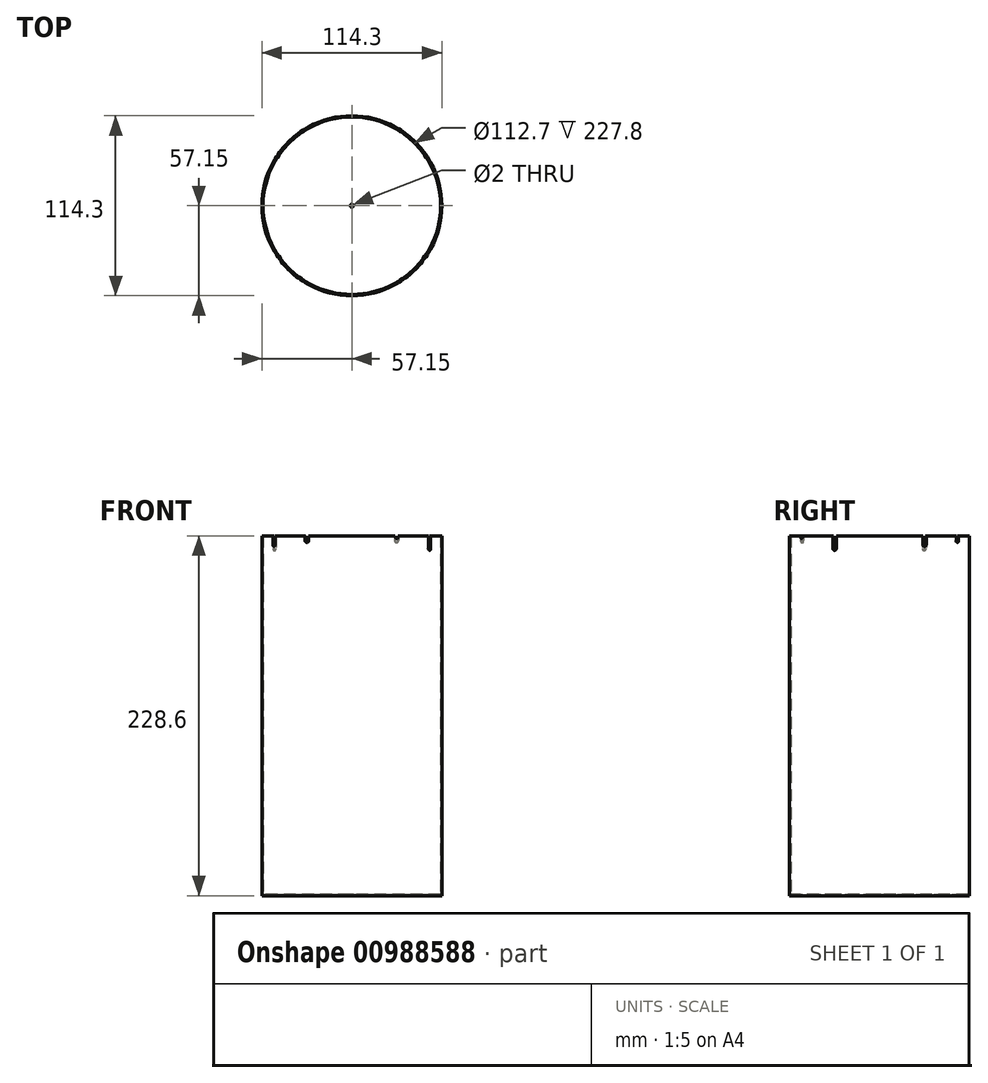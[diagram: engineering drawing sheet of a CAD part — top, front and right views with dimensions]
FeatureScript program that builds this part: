
annotation { "Feature Type Name" : "Feature", "Feature Type Description" : "" }
export const myFeature = defineFeature(function(context is Context, id is Id, definition is map)
    precondition{}
    {
        {
            var Q0;
            Q0=qCreatedBy(makeId("Top.planeOp"),FACE);
            var sketch = newSketch(context, id + "F0", { "sketchPlane" : qUnion([Q0])});
            skCircle(sketch, "E0", {"center": v(0, 0) * mm, "radius": 57.15 * mm});
            skSolve(sketch);
        }
        {
            var Q0;
            Q0=makeQuery(id+"F0.imprint","IMPRINT",FACE,{"disambiguationData":[TD([[makeQuery(id+"F0.imprint","IMPRINT",EDGE,{"derivedFrom":sQuery(id+"F0.wireOp",EDGE,"E0")}),1.0]])]});
            extrude(context, id + "F1", {"entities" : qUnion([Q0]), "depth" : 228.6 * mm, "offsetDistance" : 25.4 * mm});
        }
        {
            var Q0;
            Q0=makeQuery(id+"F1.opExtrude","CAP_FACE",FACE,{"disambiguationData":[OSD([sQuery(id+"F0.wireOp",EDGE,"E0")])],"isStart":false});
            shell(context, id + "F2", {"entities" : qUnion([Q0]), "thickness" : 0.8 * mm});
        }
        {
            var Q0;
            Q0=makeQuery(id+"F1.opExtrude","CAP_FACE",FACE,{"disambiguationData":[OSD([sQuery(id+"F0.wireOp",EDGE,"E0")])],"isStart":false});
            var sketch = newSketch(context, id + "F3", { "sketchPlane" : qUnion([Q0])});
            skLineSegment(sketch, "E1", {"start": v(-49.5, 28.57) * mm, "end": v(49.5, -28.57) * mm});
            skLineSegment(sketch, "E2", {"start": v(-49.5, -28.58) * mm, "end": v(49.5, 28.58) * mm});
            skLineSegment(sketch, "E3", {"start": v(-28.58, 49.5) * mm, "end": v(28.58, -49.5) * mm});
            skLineSegment(sketch, "E4", {"start": v(28.58, 49.5) * mm, "end": v(-28.58, -49.5) * mm});
            skSolve(sketch);
        }
        {
            var Q0;
            Q0=sQuery(id+"F3.wireOp",EDGE,"E3");
            var Q1;
            Q1=sQuery(id+"F3.wireOp",VERTEX,"E3.end");
            cPlane(context, id + "F4", {"entities" : qUnion([Q0, Q1]), "cplaneType" : CPlaneType.LINE_POINT, "offset" : 25.4 * mm, "width" : 152.4 * mm, "height" : 152.4 * mm});
        }
        {
            var Q0;
            Q0=sQuery(id+"F3.wireOp",EDGE,"E2");
            var Q1;
            Q1=sQuery(id+"F3.wireOp",VERTEX,"E2.start");
            cPlane(context, id + "F5", {"entities" : qUnion([Q0, Q1]), "cplaneType" : CPlaneType.LINE_POINT, "offset" : 25.4 * mm, "width" : 152.4 * mm, "height" : 152.4 * mm});
        }
        {
            var Q0;
            Q0=sQuery(id+"F3.wireOp",EDGE,"E1");
            var Q1;
            Q1=sQuery(id+"F3.wireOp",VERTEX,"E1.start");
            cPlane(context, id + "F6", {"entities" : qUnion([Q0, Q1]), "cplaneType" : CPlaneType.LINE_POINT, "offset" : 25.4 * mm, "width" : 152.4 * mm, "height" : 152.4 * mm});
        }
        {
            var Q0;
            Q0=sQuery(id+"F3.wireOp",EDGE,"E4");
            var Q1;
            Q1=sQuery(id+"F3.wireOp",VERTEX,"E4.end");
            cPlane(context, id + "F7", {"entities" : qUnion([Q0, Q1]), "cplaneType" : CPlaneType.LINE_POINT, "offset" : 25.4 * mm, "width" : 152.4 * mm, "height" : 152.4 * mm});
        }
        {
            var Q0;
            Q0=qCreatedBy(id+"F4.planeOp",FACE);
            var sketch = newSketch(context, id + "F8", { "sketchPlane" : qUnion([Q0])});
            skLineSegment(sketch, "E5", {"start": v(-1.25, 228.6) * mm, "end": v(-1.25, 228.1) * mm});
            skLineSegment(sketch, "E6", {"start": v(1.25, 228.6) * mm, "end": v(1.25, 228.1) * mm});
            skLineSegment(sketch, "E7", {"start": v(-1.25, 228.6) * mm, "end": v(1.25, 228.6) * mm});
            skArc(sketch, "E8", {"start": v(-1.25, 228.1) * mm, "mid": v(0, 226.85) * mm, "end": v(1.25, 228.1) * mm});
            skSolve(sketch);
        }
        {
            var Q0;
            Q0=makeQuery(id+"F8.imprint","IMPRINT",FACE,{"disambiguationData":[TD([[makeQuery(id+"F8.imprint","IMPRINT",EDGE,{"derivedFrom":sQuery(id+"F8.wireOp",EDGE,"E5")}),1.0]])]});
            var Q1;
            Q1=sQuery(id+"F3.wireOp",EDGE,"E3");
            sweep(context, id + "F9", {"operationType" : NewBodyOperationType.REMOVE, "profiles" : qUnion([Q0]), "path" : qUnion([Q1])});
        }
        {
            var Q0;
            Q0=qCreatedBy(id+"F7.planeOp",FACE);
            var sketch = newSketch(context, id + "F10", { "sketchPlane" : qUnion([Q0])});
            skLineSegment(sketch, "E9", {"start": v(-1.25, 228.6) * mm, "end": v(-1.25, 225.6) * mm});
            skLineSegment(sketch, "E10", {"start": v(1.25, 228.6) * mm, "end": v(1.25, 225.6) * mm});
            skLineSegment(sketch, "E11", {"start": v(-1.25, 228.6) * mm, "end": v(1.25, 228.6) * mm});
            skArc(sketch, "E12", {"start": v(-1.25, 225.6) * mm, "mid": v(0, 224.35) * mm, "end": v(1.25, 225.6) * mm});
            skSolve(sketch);
        }
        {
            var Q0;
            Q0=makeQuery(id+"F10.imprint","IMPRINT",FACE,{"disambiguationData":[TD([[makeQuery(id+"F10.imprint","IMPRINT",EDGE,{"derivedFrom":sQuery(id+"F10.wireOp",EDGE,"E9")}),1.0]])]});
            var Q1;
            Q1=sQuery(id+"F3.wireOp",EDGE,"E4");
            sweep(context, id + "F11", {"operationType" : NewBodyOperationType.REMOVE, "profiles" : qUnion([Q0]), "path" : qUnion([Q1])});
        }
        {
            var Q0;
            Q0=qCreatedBy(id+"F5.planeOp",FACE);
            var sketch = newSketch(context, id + "F12", { "sketchPlane" : qUnion([Q0])});
            skLineSegment(sketch, "E13", {"start": v(-1.25, 228.6) * mm, "end": v(-1.25, 223.1) * mm});
            skLineSegment(sketch, "E14", {"start": v(1.25, 228.6) * mm, "end": v(1.25, 223.1) * mm});
            skLineSegment(sketch, "E15", {"start": v(-1.25, 228.6) * mm, "end": v(1.25, 228.6) * mm});
            skArc(sketch, "E16", {"start": v(-1.25, 223.1) * mm, "mid": v(0, 221.85) * mm, "end": v(1.25, 223.1) * mm});
            skSolve(sketch);
        }
        {
            var Q0;
            Q0=makeQuery(id+"F12.imprint","IMPRINT",FACE,{"disambiguationData":[TD([[makeQuery(id+"F12.imprint","IMPRINT",EDGE,{"derivedFrom":sQuery(id+"F12.wireOp",EDGE,"E13")}),1.0]])]});
            var Q1;
            Q1=sQuery(id+"F3.wireOp",EDGE,"E2");
            sweep(context, id + "F13", {"operationType" : NewBodyOperationType.REMOVE, "profiles" : qUnion([Q0]), "path" : qUnion([Q1])});
        }
        {
            var Q0;
            Q0=qCreatedBy(id+"F6.planeOp",FACE);
            var sketch = newSketch(context, id + "F14", { "sketchPlane" : qUnion([Q0])});
            skLineSegment(sketch, "E17", {"start": v(-1.25, 228.6) * mm, "end": v(-1.25, 220.6) * mm});
            skLineSegment(sketch, "E18", {"start": v(1.25, 228.6) * mm, "end": v(1.25, 220.6) * mm});
            skLineSegment(sketch, "E19", {"start": v(-1.25, 228.6) * mm, "end": v(1.25, 228.6) * mm});
            skArc(sketch, "E20", {"start": v(-1.25, 220.6) * mm, "mid": v(0, 219.35) * mm, "end": v(1.25, 220.6) * mm});
            skSolve(sketch);
        }
        {
            var Q0;
            Q0=makeQuery(id+"F14.imprint","IMPRINT",FACE,{"disambiguationData":[TD([[makeQuery(id+"F14.imprint","IMPRINT",EDGE,{"derivedFrom":sQuery(id+"F14.wireOp",EDGE,"E17")}),1.0]])]});
            var Q1;
            Q1=sQuery(id+"F3.wireOp",EDGE,"E1");
            sweep(context, id + "F15", {"operationType" : NewBodyOperationType.REMOVE, "profiles" : qUnion([Q0]), "path" : qUnion([Q1])});
        }
        {
            var Q0;
            {var subQ0=sQuery(id+"F0.wireOp",EDGE,"E0");Q0=makeQuery(id+"F2.opShell","OFFSET_FACE",FACE,{"disambiguationData":[OSD([subQ0]),TDD([makeQuery(id+"F1.opExtrude","CAP_FACE",FACE,{"disambiguationData":[OSD([subQ0])],"isStart":true})])]});}
            var sketch = newSketch(context, id + "F16", { "sketchPlane" : qUnion([Q0])});
            skCircle(sketch, "E21", {"center": v(0, 0) * mm, "radius": 1 * mm});
            skSolve(sketch);
        }
        {
            var Q0;
            Q0 = qSketchRegion(id + "F16", true);
            extrude(context, id + "F17", {"entities" : qUnion([Q0]), "operationType" : NewBodyOperationType.REMOVE, "endBound" : BoundingType.UP_TO_NEXT, "oppositeDirection" : true, "depth" : 25.4 * mm, "offsetDistance" : 25.4 * mm});
        }
    });
